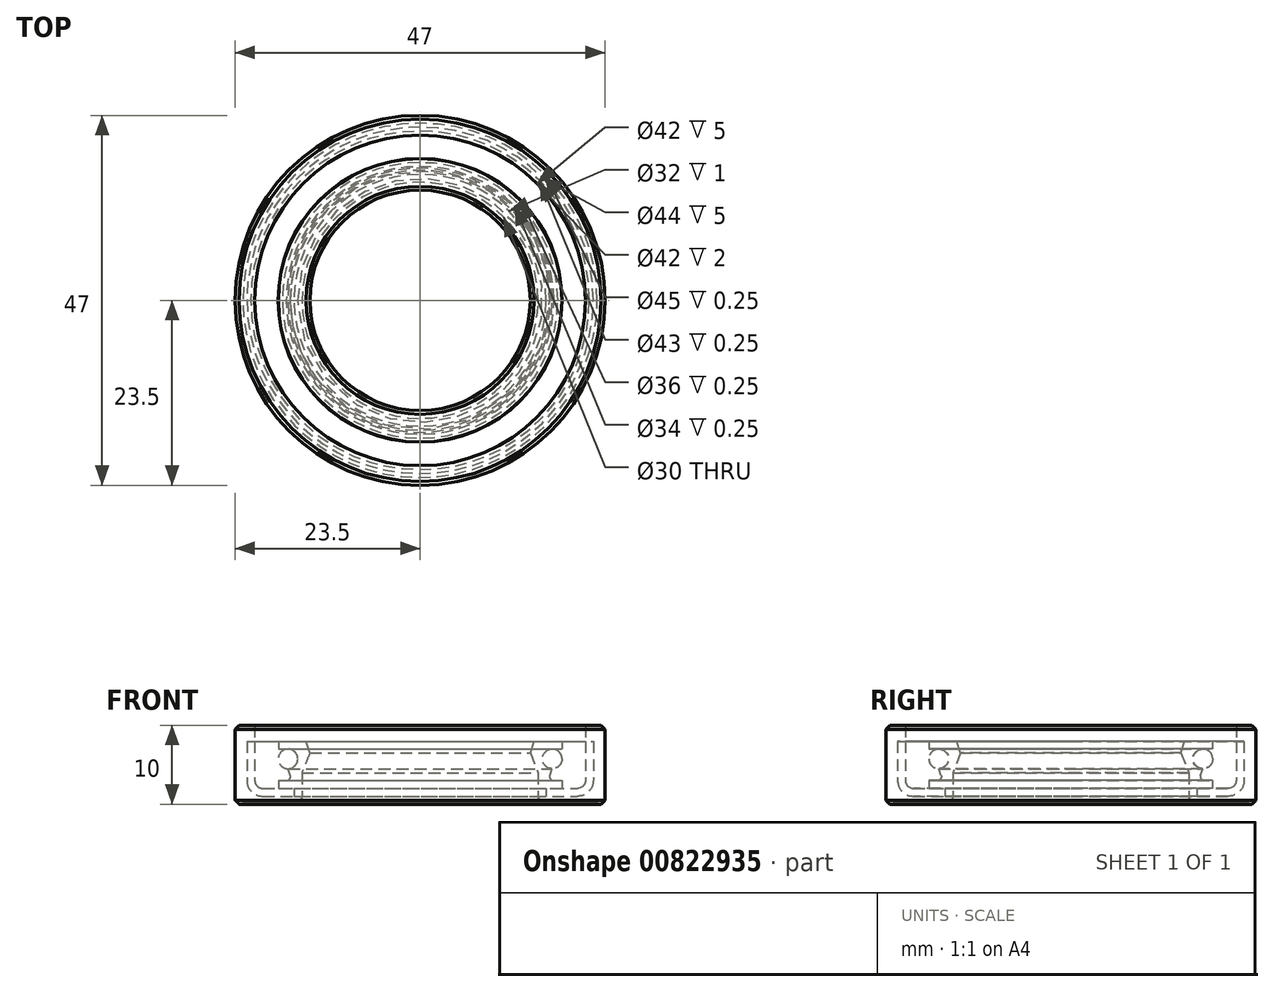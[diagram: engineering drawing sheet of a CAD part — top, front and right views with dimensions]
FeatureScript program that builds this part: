
annotation { "Feature Type Name" : "Feature", "Feature Type Description" : "" }
export const myFeature = defineFeature(function(context is Context, id is Id, definition is map)
    precondition{}
    {
        {
            var Q0;
            Q0=qCreatedBy(makeId("Front.planeOp"),FACE);
            var sketch = newSketch(context, id + "F0", { "sketchPlane" : qUnion([Q0])});
            skLineSegment(sketch, "E0", {"start": v(-14, 0) * mm, "end": v(-14, 10) * mm, "construction": true});
            skLineSegment(sketch, "E1", {"start": v(-14, 10) * mm, "end": v(-23.5, 10) * mm, "construction": true});
            skLineSegment(sketch, "E2", {"start": v(0, 0) * mm, "end": v(-14, 0) * mm, "construction": true});
            skLineSegment(sketch, "E3", {"start": v(0, 0) * mm, "end": v(0, 17.8) * mm, "construction": true});
            skLineSegment(sketch, "E4", {"start": v(-23, 10) * mm, "end": v(-23.5, 9.5) * mm});
            skLineSegment(sketch, "E5", {"start": v(-23.5, 9.5) * mm, "end": v(-23.5, 0.5) * mm});
            skLineSegment(sketch, "E6", {"start": v(-23.5, 0.5) * mm, "end": v(-23, 0) * mm});
            skLineSegment(sketch, "E7", {"start": v(-23, 0) * mm, "end": v(-16, 0) * mm, "construction": true});
            skLineSegment(sketch, "E8", {"start": v(-15, 1) * mm, "end": v(-15, 4) * mm});
            skLineSegment(sketch, "E9", {"start": v(-15, 4) * mm, "end": v(-14, 6.5) * mm});
            skLineSegment(sketch, "E10", {"start": v(-14, 6.5) * mm, "end": v(-14.48, 8) * mm});
            skLineSegment(sketch, "E11", {"start": v(-14.48, 8) * mm, "end": v(-18, 8) * mm});
            skLineSegment(sketch, "E12", {"start": v(-18, 8) * mm, "end": v(-18, 7) * mm});
            skLineSegment(sketch, "E13", {"start": v(-18, 7) * mm, "end": v(-16.78, 7) * mm});
            skLineSegment(sketch, "E14", {"start": v(-16.14, 7) * mm, "end": v(-16.14, 4.5) * mm, "construction": true});
            skLineSegment(sketch, "E15", {"start": v(-16.14, 4.5) * mm, "end": v(-16.78, 4.5) * mm, "construction": true});
            skLineSegment(sketch, "E16", {"start": v(-16.95, 3) * mm, "end": v(-18, 3) * mm});
            skLineSegment(sketch, "E17", {"start": v(-18, 3) * mm, "end": v(-18, 2) * mm});
            skLineSegment(sketch, "E18", {"start": v(-18, 2) * mm, "end": v(-16, 2) * mm});
            skLineSegment(sketch, "E19", {"start": v(-16, 2) * mm, "end": v(-16, 1) * mm});
            skLineSegment(sketch, "E20", {"start": v(-16, 1) * mm, "end": v(-20, 1) * mm});
            skLineSegment(sketch, "E21", {"start": v(-22, 3) * mm, "end": v(-22, 8) * mm});
            skLineSegment(sketch, "E22", {"start": v(-22, 8) * mm, "end": v(-21, 8) * mm});
            skLineSegment(sketch, "E23", {"start": v(-21, 8) * mm, "end": v(-21, 10) * mm});
            skLineSegment(sketch, "E24", {"start": v(-21, 10) * mm, "end": v(-23, 10) * mm});
            skLineSegment(sketch, "E25", {"start": v(-21, 8) * mm, "end": v(-21, 3) * mm});
            skLineSegment(sketch, "E26", {"start": v(-20, 2) * mm, "end": v(-18, 2) * mm});
            skPoint(sketch, "E27.visualSharp", {"position": v(-21, 2) * mm});
            skArc(sketch, "E27.filletArc", {"start": v(-21, 3) * mm, "mid": v(-20.7, 2.3) * mm, "end": v(-20, 2) * mm});
            skPoint(sketch, "E28.visualSharp", {"position": v(-22, 1) * mm});
            skArc(sketch, "E28.filletArc", {"start": v(-22, 3) * mm, "mid": v(-21.41, 1.59) * mm, "end": v(-20, 1) * mm});
            skPoint(sketch, "E29.visualSharp", {"position": v(-15, 0) * mm});
            skArc(sketch, "E29.filletArc", {"start": v(-16, 0) * mm, "mid": v(-15.3, 0.3) * mm, "end": v(-15, 1) * mm});
            skLineSegment(sketch, "E30", {"start": v(-16.78, 4.5) * mm, "end": v(-16.48, 3.67) * mm});
            skLineSegment(sketch, "E31", {"start": v(-16.78, 4.5) * mm, "end": v(-16.78, 7) * mm, "construction": true});
            skCircle(sketch, "E32", {"center": v(-16.78, 5.75) * mm, "radius": 1.25 * mm});
            skPoint(sketch, "E33.visualSharp", {"position": v(-16.25, 3) * mm});
            skArc(sketch, "E33.filletArc", {"start": v(-16.95, 3) * mm, "mid": v(-16.55, 3.21) * mm, "end": v(-16.48, 3.67) * mm});
            skLineSegment(sketch, "E34", {"start": v(-23, 0) * mm, "end": v(-22.5, 0) * mm});
            skLineSegment(sketch, "E35", {"start": v(-22.5, 0) * mm, "end": v(-22.5, 0.25) * mm});
            skLineSegment(sketch, "E36", {"start": v(-22.5, 0.25) * mm, "end": v(-22, 0.25) * mm});
            skLineSegment(sketch, "E37", {"start": v(-22, 0.25) * mm, "end": v(-22, 0) * mm});
            skLineSegment(sketch, "E38", {"start": v(-22, 0) * mm, "end": v(-21.5, 0) * mm});
            skLineSegment(sketch, "E39", {"start": v(-21.5, 0) * mm, "end": v(-21.5, 0.25) * mm});
            skLineSegment(sketch, "E40", {"start": v(-21.5, 0.25) * mm, "end": v(-21, 0.25) * mm});
            skLineSegment(sketch, "E41", {"start": v(-21, 0.25) * mm, "end": v(-21, 0) * mm});
            skLineSegment(sketch, "E42", {"start": v(-21, 0) * mm, "end": v(-18, 0) * mm});
            skLineSegment(sketch, "E43", {"start": v(-18, 0) * mm, "end": v(-18, 0.25) * mm});
            skPoint(sketch, "E43.endSnap0", {"position": v(-21.25, 0.25) * mm});
            skLineSegment(sketch, "E44", {"start": v(-18, 0.25) * mm, "end": v(-17.5, 0.25) * mm});
            skLineSegment(sketch, "E45", {"start": v(-17.5, 0.25) * mm, "end": v(-17.5, 0) * mm});
            skLineSegment(sketch, "E46", {"start": v(-17.5, 0) * mm, "end": v(-17, 0) * mm});
            skLineSegment(sketch, "E47", {"start": v(-17, 0) * mm, "end": v(-17, 0.25) * mm});
            skLineSegment(sketch, "E48", {"start": v(-17, 0.25) * mm, "end": v(-16.5, 0.25) * mm});
            skLineSegment(sketch, "E49", {"start": v(-16.5, 0.25) * mm, "end": v(-16.5, 0) * mm});
            skLineSegment(sketch, "E50", {"start": v(-16.5, 0) * mm, "end": v(-16, 0) * mm});
            skSolve(sketch);
        }
        {
            var Q0;
            {var subQ0=sQuery(id+"F0.wireOp",EDGE,"E32");var subQ1=makeQuery(id+"F0.imprint","INTERSECT",VERTEX,{"derivedFrom":[sQuery(id+"F0.wireOp",EDGE,"E13"),subQ0]});Q0=makeQuery(id+"F0.imprint","IMPRINT",FACE,{"disambiguationData":[TD([[makeQuery(id+"F0.imprint","IMPRINT",EDGE,{"disambiguationData":[TD([[subQ1,-1.0]])],"derivedFrom":subQ0}),1.0]])]});}
            var Q1;
            Q1=sQuery(id+"F0.wireOp",EDGE,"E3");
            revolve(context, id + "F1", {"surfaceOperationType" : NewSurfaceOperationType.NEW, "entities" : qUnion([Q0]), "axis" : qUnion([Q1]), "revolveType" : RevolveType.FULL});
        }
        {
            var Q0;
            Q0=makeQuery(id+"F0.imprint","IMPRINT",FACE,{"disambiguationData":[TD([[makeQuery(id+"F0.imprint","IMPRINT",EDGE,{"derivedFrom":sQuery(id+"F0.wireOp",EDGE,"E18")}),-1.0]])]});
            var Q1;
            Q1=sQuery(id+"F0.wireOp",EDGE,"E3");
            revolve(context, id + "F2", {"surfaceOperationType" : NewSurfaceOperationType.NEW, "entities" : qUnion([Q0]), "axis" : qUnion([Q1]), "revolveType" : RevolveType.FULL});
        }
        {
            var Q0;
            Q0=makeQuery(id+"F0.imprint","IMPRINT",FACE,{"disambiguationData":[TD([[makeQuery(id+"F0.imprint","IMPRINT",EDGE,{"derivedFrom":sQuery(id+"F0.wireOp",EDGE,"E4")}),1.0]])]});
            var Q1;
            Q1=sQuery(id+"F0.wireOp",EDGE,"E3");
            revolve(context, id + "F3", {"surfaceOperationType" : NewSurfaceOperationType.NEW, "entities" : qUnion([Q0]), "axis" : qUnion([Q1]), "revolveType" : RevolveType.FULL});
        }
    });
